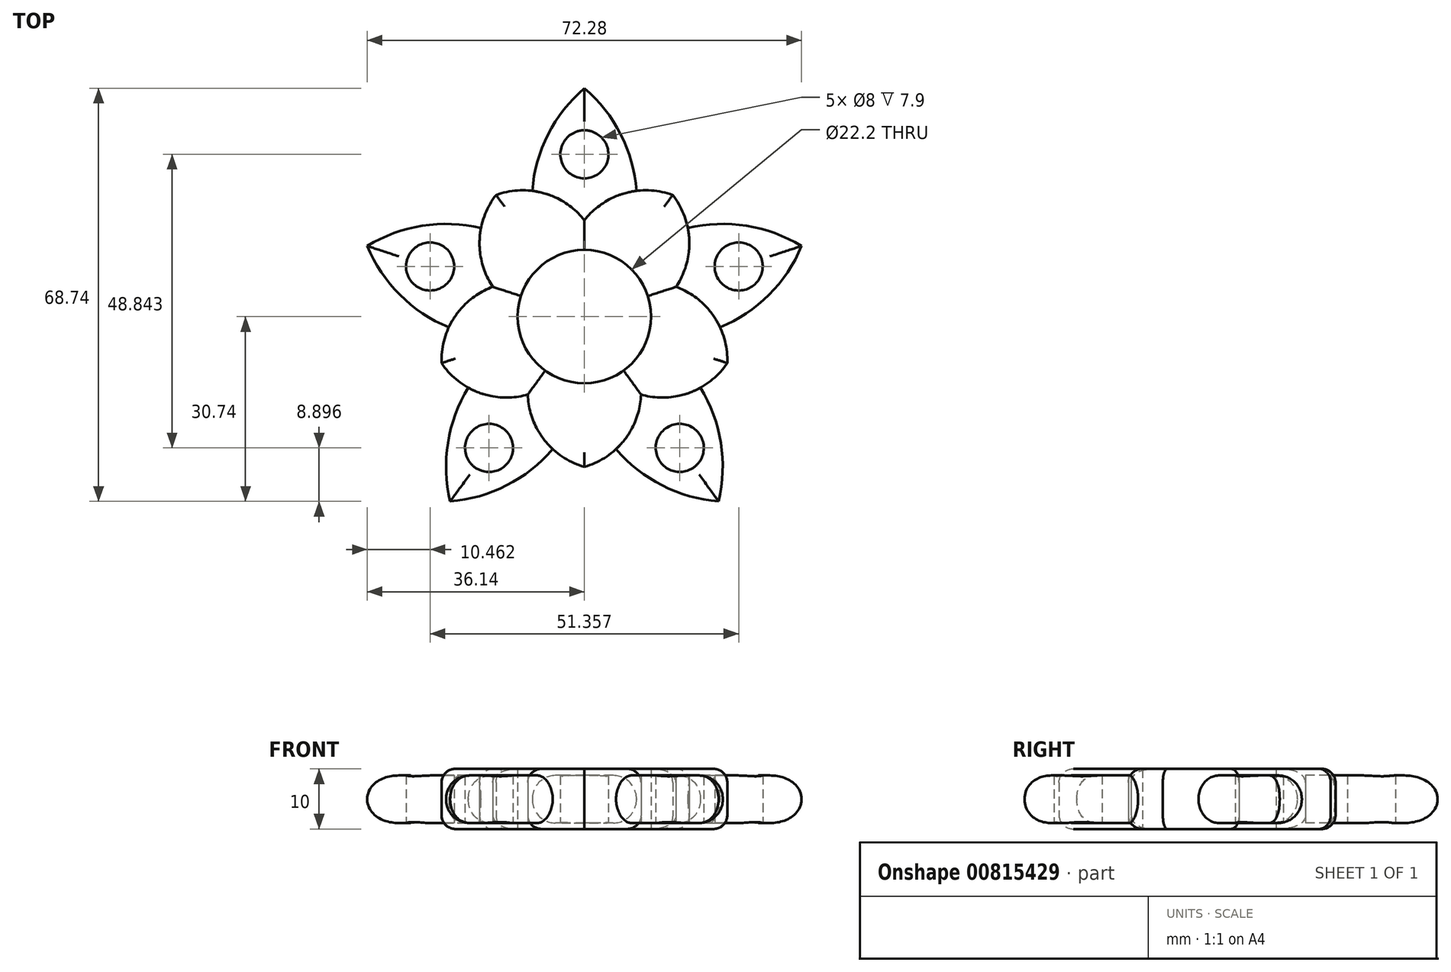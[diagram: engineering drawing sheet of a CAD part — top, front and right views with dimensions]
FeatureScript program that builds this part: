
annotation { "Feature Type Name" : "Feature", "Feature Type Description" : "" }
export const myFeature = defineFeature(function(context is Context, id is Id, definition is map)
    precondition{}
    {
        {
            var Q0;
            Q0=qCreatedBy(makeId("Top.planeOp"),FACE);
            var sketch = newSketch(context, id + "F0", { "sketchPlane" : qUnion([Q0])});
            skLineSegment(sketch, "E0", {"start": v(0, 0) * mm, "end": v(0, 38) * mm, "construction": true});
            skArc(sketch, "E1", {"start": v(0, 38) * mm, "mid": v(-8.75, 19) * mm, "end": v(0, 0) * mm});
            skArc(sketch, "E2", {"start": v(0, 0) * mm, "mid": v(8.75, 19) * mm, "end": v(0, 38) * mm});
            skLineSegment(sketch, "E3", {"start": v(0, 0) * mm, "end": v(0, -25) * mm, "construction": true});
            skArc(sketch, "E4", {"start": v(0, -25) * mm, "mid": v(9.43, -12.5) * mm, "end": v(0, 0) * mm});
            skArc(sketch, "E5", {"start": v(0, 0) * mm, "mid": v(-9.43, -12.5) * mm, "end": v(0, -25) * mm});
            skCircle(sketch, "E6", {"center": v(0, 0) * mm, "radius": 11.1 * mm});
            skArc(sketch, "E7.1.0", {"start": v(0, 0) * mm, "mid": v(-15.37, 14.2) * mm, "end": v(-36.14, 11.74) * mm});
            skArc(sketch, "E7.1.1", {"start": v(-36.14, 11.74) * mm, "mid": v(-20.77, -2.45) * mm, "end": v(0, 0) * mm});
            skArc(sketch, "E7.1.2", {"start": v(0, 0) * mm, "mid": v(8.97, -12.83) * mm, "end": v(23.78, -7.73) * mm});
            skArc(sketch, "E7.1.3", {"start": v(23.78, -7.73) * mm, "mid": v(14.8, 5.1) * mm, "end": v(0, 0) * mm});
            skArc(sketch, "E7.2.0", {"start": v(0, 0) * mm, "mid": v(-18.25, -10.23) * mm, "end": v(-22.34, -30.74) * mm});
            skArc(sketch, "E7.2.1", {"start": v(-22.34, -30.74) * mm, "mid": v(-4.09, -20.52) * mm, "end": v(0, 0) * mm});
            skArc(sketch, "E7.2.2", {"start": v(0, 0) * mm, "mid": v(14.98, 4.57) * mm, "end": v(14.7, 20.23) * mm});
            skArc(sketch, "E7.2.3", {"start": v(14.7, 20.23) * mm, "mid": v(-0.28, 15.66) * mm, "end": v(0, 0) * mm});
            skArc(sketch, "E7.3.0", {"start": v(0, 0) * mm, "mid": v(4.09, -20.52) * mm, "end": v(22.34, -30.74) * mm});
            skArc(sketch, "E7.3.1", {"start": v(22.34, -30.74) * mm, "mid": v(18.25, -10.23) * mm, "end": v(0, 0) * mm});
            skArc(sketch, "E7.3.2", {"start": v(0, 0) * mm, "mid": v(0.28, 15.66) * mm, "end": v(-14.7, 20.23) * mm});
            skArc(sketch, "E7.3.3", {"start": v(-14.7, 20.23) * mm, "mid": v(-14.98, 4.57) * mm, "end": v(0, 0) * mm});
            skArc(sketch, "E7.4.0", {"start": v(0, 0) * mm, "mid": v(20.77, -2.45) * mm, "end": v(36.14, 11.74) * mm});
            skArc(sketch, "E7.4.1", {"start": v(36.14, 11.74) * mm, "mid": v(15.37, 14.2) * mm, "end": v(0, 0) * mm});
            skArc(sketch, "E7.4.2", {"start": v(0, 0) * mm, "mid": v(-14.8, 5.1) * mm, "end": v(-23.78, -7.73) * mm});
            skArc(sketch, "E7.4.3", {"start": v(-23.78, -7.73) * mm, "mid": v(-8.97, -12.83) * mm, "end": v(0, 0) * mm});
            skCircle(sketch, "E8", {"center": v(0, 27) * mm, "radius": 4 * mm});
            skCircle(sketch, "E9.1.0", {"center": v(-25.68, 8.34) * mm, "radius": 4 * mm});
            skCircle(sketch, "E9.2.0", {"center": v(-15.87, -21.84) * mm, "radius": 4 * mm});
            skCircle(sketch, "E9.3.0", {"center": v(15.87, -21.84) * mm, "radius": 4 * mm});
            skCircle(sketch, "E9.4.0", {"center": v(25.68, 8.34) * mm, "radius": 4 * mm});
            skSolve(sketch);
        }
        {
            var Q0;
            {var subQ0=sQuery(id+"F0.wireOp",EDGE,"E2");var subQ1=sQuery(id+"F0.wireOp",EDGE,"E1");var subQ2=makeQuery(id+"F0.imprint","INTERSECT",VERTEX,{"derivedFrom":[subQ1,subQ0]});Q0=makeQuery(id+"F0.imprint","IMPRINT",FACE,{"disambiguationData":[TD([[makeQuery(id+"F0.imprint","IMPRINT",EDGE,{"disambiguationData":[TD([[subQ2,-1.0]])],"derivedFrom":subQ1}),1.0]])]});}
            var Q1;
            {var subQ0=sQuery(id+"F0.wireOp",EDGE,"E7.3.0");var subQ1=sQuery(id+"F0.wireOp",EDGE,"E4");var subQ2=makeQuery(id+"F0.imprint","INTERSECT",VERTEX,{"derivedFrom":[subQ1,subQ0]});Q1=makeQuery(id+"F0.imprint","IMPRINT",FACE,{"disambiguationData":[TD([[makeQuery(id+"F0.imprint","IMPRINT",EDGE,{"disambiguationData":[TD([[subQ2,-1.0]])],"derivedFrom":subQ1}),-1.0]])]});}
            var Q2;
            {var subQ0=sQuery(id+"F0.wireOp",EDGE,"E7.2.1");var subQ1=sQuery(id+"F0.wireOp",EDGE,"E5");var subQ2=makeQuery(id+"F0.imprint","INTERSECT",VERTEX,{"derivedFrom":[subQ1,subQ0]});Q2=makeQuery(id+"F0.imprint","IMPRINT",FACE,{"disambiguationData":[TD([[makeQuery(id+"F0.imprint","IMPRINT",EDGE,{"disambiguationData":[TD([[subQ2,1.0]])],"derivedFrom":subQ1}),-1.0]])]});}
            var Q3;
            {var subQ0=sQuery(id+"F0.wireOp",EDGE,"E7.1.1");var subQ1=sQuery(id+"F0.wireOp",EDGE,"E7.1.0");var subQ2=makeQuery(id+"F0.imprint","INTERSECT",VERTEX,{"derivedFrom":[subQ1,subQ0]});Q3=makeQuery(id+"F0.imprint","IMPRINT",FACE,{"disambiguationData":[TD([[makeQuery(id+"F0.imprint","IMPRINT",EDGE,{"disambiguationData":[TD([[subQ2,1.0]])],"derivedFrom":subQ1}),1.0]])]});}
            var Q4;
            {var subQ0=sQuery(id+"F0.wireOp",EDGE,"E7.4.0");var subQ1=sQuery(id+"F0.wireOp",EDGE,"E7.1.3");var subQ2=makeQuery(id+"F0.imprint","INTERSECT",VERTEX,{"derivedFrom":[subQ1,subQ0]});Q4=makeQuery(id+"F0.imprint","IMPRINT",FACE,{"disambiguationData":[TD([[makeQuery(id+"F0.imprint","IMPRINT",EDGE,{"disambiguationData":[TD([[subQ2,-1.0]])],"derivedFrom":subQ1}),-1.0]])]});}
            extrude(context, id + "F1", {"entities" : qUnion([Q0, Q1, Q2, Q3, Q4]), "depth" : 3.9 * mm, "offsetDistance" : 25 * mm, "hasSecondDirection" : true, "secondDirectionOppositeDirection" : true, "secondDirectionDepth" : 4 * mm});
        }
        {
            var Q0;
            {var subQ0=sQuery(id+"F0.wireOp",EDGE,"E7.3.2");var subQ1=sQuery(id+"F0.wireOp",EDGE,"E1");var subQ2=makeQuery(id+"F0.imprint","INTERSECT",VERTEX,{"derivedFrom":[subQ1,subQ0]});Q0=makeQuery(id+"F0.imprint","IMPRINT",FACE,{"disambiguationData":[TD([[makeQuery(id+"F0.imprint","IMPRINT",EDGE,{"disambiguationData":[TD([[subQ2,-1.0]])],"derivedFrom":subQ1}),-1.0]])]});}
            var Q1;
            {var subQ1=sQuery(id+"F0.wireOp",EDGE,"E1");var subQ7=sQuery(id+"F0.wireOp",EDGE,"E7.3.2");var subQ9=makeQuery(id+"F0.imprint","INTERSECT",VERTEX,{"derivedFrom":[subQ1,subQ7]});Q1=makeQuery(id+"F0.imprint","IMPRINT",FACE,{"disambiguationData":[TD([[makeQuery(id+"F0.imprint","IMPRINT",EDGE,{"disambiguationData":[TD([[subQ9,-1.0]])],"derivedFrom":subQ1}),1.0]])]});}
            var Q2;
            {var subQ1=sQuery(id+"F0.wireOp",EDGE,"E7.1.0");var subQ5=sQuery(id+"F0.wireOp",EDGE,"E1");var subQ6=makeQuery(id+"F0.imprint","INTERSECT",VERTEX,{"derivedFrom":[subQ5,subQ1]});Q2=makeQuery(id+"F0.imprint","IMPRINT",FACE,{"disambiguationData":[TD([[makeQuery(id+"F0.imprint","IMPRINT",EDGE,{"disambiguationData":[TD([[subQ6,-1.0]])],"derivedFrom":subQ5}),-1.0]])]});}
            var Q3;
            {var subQ1=sQuery(id+"F0.wireOp",EDGE,"E7.1.2");var subQ3=sQuery(id+"F0.wireOp",EDGE,"E4");var subQ4=makeQuery(id+"F0.imprint","INTERSECT",VERTEX,{"derivedFrom":[subQ3,subQ1]});Q3=makeQuery(id+"F0.imprint","IMPRINT",FACE,{"disambiguationData":[TD([[makeQuery(id+"F0.imprint","IMPRINT",EDGE,{"disambiguationData":[TD([[subQ4,-1.0]])],"derivedFrom":subQ3}),-1.0]])]});}
            var Q4;
            {var subQ5=sQuery(id+"F0.wireOp",EDGE,"E6");var subQ6=sQuery(id+"F0.wireOp",EDGE,"E5");var subQ7=makeQuery(id+"F0.imprint","INTERSECT",VERTEX,{"derivedFrom":[subQ6,subQ5]});Q4=makeQuery(id+"F0.imprint","IMPRINT",FACE,{"disambiguationData":[TD([[makeQuery(id+"F0.imprint","IMPRINT",EDGE,{"disambiguationData":[TD([[subQ7,-1.0]])],"derivedFrom":subQ6}),-1.0]])]});}
            var Q5;
            {var subQ1=sQuery(id+"F0.wireOp",EDGE,"E6");var subQ5=sQuery(id+"F0.wireOp",EDGE,"E7.2.2");var subQ6=makeQuery(id+"F0.imprint","INTERSECT",VERTEX,{"derivedFrom":[subQ1,subQ5]});Q5=makeQuery(id+"F0.imprint","IMPRINT",FACE,{"disambiguationData":[TD([[makeQuery(id+"F0.imprint","IMPRINT",EDGE,{"disambiguationData":[TD([[subQ6,1.0]])],"derivedFrom":subQ1}),-1.0]])]});}
            var Q6;
            {var subQ0=sQuery(id+"F0.wireOp",EDGE,"E5");var subQ1=sQuery(id+"F0.wireOp",EDGE,"E4");var subQ2=makeQuery(id+"F0.imprint","INTERSECT",VERTEX,{"derivedFrom":[subQ1,subQ0]});Q6=makeQuery(id+"F0.imprint","IMPRINT",FACE,{"disambiguationData":[TD([[makeQuery(id+"F0.imprint","IMPRINT",EDGE,{"disambiguationData":[TD([[subQ2,-1.0]])],"derivedFrom":subQ1}),1.0]])]});}
            var Q7;
            {var subQ0=sQuery(id+"F0.wireOp",EDGE,"E7.4.2");var subQ1=sQuery(id+"F0.wireOp",EDGE,"E7.1.1");var subQ2=makeQuery(id+"F0.imprint","INTERSECT",VERTEX,{"derivedFrom":[subQ1,subQ0]});Q7=makeQuery(id+"F0.imprint","IMPRINT",FACE,{"disambiguationData":[TD([[makeQuery(id+"F0.imprint","IMPRINT",EDGE,{"disambiguationData":[TD([[subQ2,-1.0]])],"derivedFrom":subQ1}),-1.0]])]});}
            var Q8;
            {var subQ0=sQuery(id+"F0.wireOp",EDGE,"E7.1.2");var subQ1=sQuery(id+"F0.wireOp",EDGE,"E4");var subQ2=makeQuery(id+"F0.imprint","INTERSECT",VERTEX,{"derivedFrom":[subQ1,subQ0]});Q8=makeQuery(id+"F0.imprint","IMPRINT",FACE,{"disambiguationData":[TD([[makeQuery(id+"F0.imprint","IMPRINT",EDGE,{"disambiguationData":[TD([[subQ2,-1.0]])],"derivedFrom":subQ1}),1.0]])]});}
            var Q9;
            {var subQ0=sQuery(id+"F0.wireOp",EDGE,"E7.3.3");var subQ1=sQuery(id+"F0.wireOp",EDGE,"E6");var subQ2=makeQuery(id+"F0.imprint","INTERSECT",VERTEX,{"derivedFrom":[subQ1,subQ0]});Q9=makeQuery(id+"F0.imprint","IMPRINT",FACE,{"disambiguationData":[TD([[makeQuery(id+"F0.imprint","IMPRINT",EDGE,{"disambiguationData":[TD([[subQ2,-1.0]])],"derivedFrom":subQ1}),-1.0]])]});}
            var Q10;
            {var subQ0=sQuery(id+"F0.wireOp",EDGE,"E7.1.3");var subQ1=sQuery(id+"F0.wireOp",EDGE,"E7.1.2");var subQ2=makeQuery(id+"F0.imprint","INTERSECT",VERTEX,{"derivedFrom":[subQ1,subQ0]});Q10=makeQuery(id+"F0.imprint","IMPRINT",FACE,{"disambiguationData":[TD([[makeQuery(id+"F0.imprint","IMPRINT",EDGE,{"disambiguationData":[TD([[subQ2,1.0]])],"derivedFrom":subQ1}),1.0]])]});}
            var Q11;
            {var subQ1=sQuery(id+"F0.wireOp",EDGE,"E4");var subQ5=sQuery(id+"F0.wireOp",EDGE,"E7.3.0");var subQ6=makeQuery(id+"F0.imprint","INTERSECT",VERTEX,{"derivedFrom":[subQ1,subQ5]});Q11=makeQuery(id+"F0.imprint","IMPRINT",FACE,{"disambiguationData":[TD([[makeQuery(id+"F0.imprint","IMPRINT",EDGE,{"disambiguationData":[TD([[subQ6,-1.0]])],"derivedFrom":subQ1}),1.0]])]});}
            var Q12;
            {var subQ3=sQuery(id+"F0.wireOp",EDGE,"E7.2.1");var subQ5=sQuery(id+"F0.wireOp",EDGE,"E5");var subQ6=makeQuery(id+"F0.imprint","INTERSECT",VERTEX,{"derivedFrom":[subQ5,subQ3]});Q12=makeQuery(id+"F0.imprint","IMPRINT",FACE,{"disambiguationData":[TD([[makeQuery(id+"F0.imprint","IMPRINT",EDGE,{"disambiguationData":[TD([[subQ6,1.0]])],"derivedFrom":subQ5}),1.0]])]});}
            var Q13;
            {var subQ0=sQuery(id+"F0.wireOp",EDGE,"E6");var subQ1=sQuery(id+"F0.wireOp",EDGE,"E5");var subQ2=makeQuery(id+"F0.imprint","INTERSECT",VERTEX,{"derivedFrom":[subQ1,subQ0]});Q13=makeQuery(id+"F0.imprint","IMPRINT",FACE,{"disambiguationData":[TD([[makeQuery(id+"F0.imprint","IMPRINT",EDGE,{"disambiguationData":[TD([[subQ2,-1.0]])],"derivedFrom":subQ1}),1.0]])]});}
            var Q14;
            {var subQ0=sQuery(id+"F0.wireOp",EDGE,"E7.1.3");var subQ1=sQuery(id+"F0.wireOp",EDGE,"E6");var subQ2=makeQuery(id+"F0.imprint","INTERSECT",VERTEX,{"derivedFrom":[subQ1,subQ0]});Q14=makeQuery(id+"F0.imprint","IMPRINT",FACE,{"disambiguationData":[TD([[makeQuery(id+"F0.imprint","IMPRINT",EDGE,{"disambiguationData":[TD([[subQ2,1.0]])],"derivedFrom":subQ1}),-1.0]])]});}
            var Q15;
            {var subQ3=sQuery(id+"F0.wireOp",EDGE,"E7.2.3");var subQ5=sQuery(id+"F0.wireOp",EDGE,"E2");var subQ6=makeQuery(id+"F0.imprint","INTERSECT",VERTEX,{"derivedFrom":[subQ5,subQ3]});Q15=makeQuery(id+"F0.imprint","IMPRINT",FACE,{"disambiguationData":[TD([[makeQuery(id+"F0.imprint","IMPRINT",EDGE,{"disambiguationData":[TD([[subQ6,1.0]])],"derivedFrom":subQ5}),1.0]])]});}
            var Q16;
            {var subQ0=sQuery(id+"F0.wireOp",EDGE,"E7.2.0");var subQ1=sQuery(id+"F0.wireOp",EDGE,"E6");var subQ2=makeQuery(id+"F0.imprint","INTERSECT",VERTEX,{"derivedFrom":[subQ1,subQ0]});Q16=makeQuery(id+"F0.imprint","IMPRINT",FACE,{"disambiguationData":[TD([[makeQuery(id+"F0.imprint","IMPRINT",EDGE,{"disambiguationData":[TD([[subQ2,-1.0]])],"derivedFrom":subQ1}),-1.0]])]});}
            var Q17;
            {var subQ0=sQuery(id+"F0.wireOp",EDGE,"E7.1.0");var subQ1=sQuery(id+"F0.wireOp",EDGE,"E1");var subQ2=makeQuery(id+"F0.imprint","INTERSECT",VERTEX,{"derivedFrom":[subQ1,subQ0]});Q17=makeQuery(id+"F0.imprint","IMPRINT",FACE,{"disambiguationData":[TD([[makeQuery(id+"F0.imprint","IMPRINT",EDGE,{"disambiguationData":[TD([[subQ2,-1.0]])],"derivedFrom":subQ1}),1.0]])]});}
            var Q18;
            {var subQ1=sQuery(id+"F0.wireOp",EDGE,"E6");var subQ7=sQuery(id+"F0.wireOp",EDGE,"E2");var subQ8=makeQuery(id+"F0.imprint","INTERSECT",VERTEX,{"derivedFrom":[subQ7,subQ1]});Q18=makeQuery(id+"F0.imprint","IMPRINT",FACE,{"disambiguationData":[TD([[makeQuery(id+"F0.imprint","IMPRINT",EDGE,{"disambiguationData":[TD([[subQ8,-1.0]])],"derivedFrom":subQ7}),-1.0]])]});}
            var Q19;
            {var subQ0=sQuery(id+"F0.wireOp",EDGE,"E7.2.3");var subQ1=sQuery(id+"F0.wireOp",EDGE,"E2");var subQ2=makeQuery(id+"F0.imprint","INTERSECT",VERTEX,{"derivedFrom":[subQ1,subQ0]});Q19=makeQuery(id+"F0.imprint","IMPRINT",FACE,{"disambiguationData":[TD([[makeQuery(id+"F0.imprint","IMPRINT",EDGE,{"disambiguationData":[TD([[subQ2,1.0]])],"derivedFrom":subQ1}),-1.0]])]});}
            var Q20;
            {var subQ0=sQuery(id+"F0.wireOp",EDGE,"E7.4.0");var subQ1=sQuery(id+"F0.wireOp",EDGE,"E6");var subQ2=makeQuery(id+"F0.imprint","INTERSECT",VERTEX,{"derivedFrom":[subQ1,subQ0]});Q20=makeQuery(id+"F0.imprint","IMPRINT",FACE,{"disambiguationData":[TD([[makeQuery(id+"F0.imprint","IMPRINT",EDGE,{"disambiguationData":[TD([[subQ2,-1.0]])],"derivedFrom":subQ1}),-1.0]])]});}
            var Q21;
            {var subQ0=sQuery(id+"F0.wireOp",EDGE,"E7.3.0");var subQ1=sQuery(id+"F0.wireOp",EDGE,"E6");var subQ2=makeQuery(id+"F0.imprint","INTERSECT",VERTEX,{"derivedFrom":[subQ1,subQ0]});Q21=makeQuery(id+"F0.imprint","IMPRINT",FACE,{"disambiguationData":[TD([[makeQuery(id+"F0.imprint","IMPRINT",EDGE,{"disambiguationData":[TD([[subQ2,-1.0]])],"derivedFrom":subQ1}),-1.0]])]});}
            var Q22;
            {var subQ0=sQuery(id+"F0.wireOp",EDGE,"E7.4.2");var subQ1=sQuery(id+"F0.wireOp",EDGE,"E6");var subQ2=makeQuery(id+"F0.imprint","INTERSECT",VERTEX,{"derivedFrom":[subQ1,subQ0]});Q22=makeQuery(id+"F0.imprint","IMPRINT",FACE,{"disambiguationData":[TD([[makeQuery(id+"F0.imprint","IMPRINT",EDGE,{"disambiguationData":[TD([[subQ2,-1.0]])],"derivedFrom":subQ1}),-1.0]])]});}
            var Q23;
            {var subQ0=sQuery(id+"F0.wireOp",EDGE,"E7.3.2");var subQ1=sQuery(id+"F0.wireOp",EDGE,"E6");var subQ2=makeQuery(id+"F0.imprint","INTERSECT",VERTEX,{"derivedFrom":[subQ1,subQ0]});Q23=makeQuery(id+"F0.imprint","IMPRINT",FACE,{"disambiguationData":[TD([[makeQuery(id+"F0.imprint","IMPRINT",EDGE,{"disambiguationData":[TD([[subQ2,-1.0]])],"derivedFrom":subQ1}),-1.0]])]});}
            var Q24;
            {var subQ0=sQuery(id+"F0.wireOp",EDGE,"E6");var subQ1=sQuery(id+"F0.wireOp",EDGE,"E2");var subQ2=makeQuery(id+"F0.imprint","INTERSECT",VERTEX,{"derivedFrom":[subQ1,subQ0]});Q24=makeQuery(id+"F0.imprint","IMPRINT",FACE,{"disambiguationData":[TD([[makeQuery(id+"F0.imprint","IMPRINT",EDGE,{"disambiguationData":[TD([[subQ2,-1.0]])],"derivedFrom":subQ1}),1.0]])]});}
            extrude(context, id + "F2", {"entities" : qUnion([Q0, Q1, Q2, Q3, Q4, Q5, Q6, Q7, Q8, Q9, Q10, Q11, Q12, Q13, Q14, Q15, Q16, Q17, Q18, Q19, Q20, Q21, Q22, Q23, Q24]), "depth" : 5 * mm, "offsetDistance" : 25 * mm, "hasSecondDirection" : true, "secondDirectionOppositeDirection" : true, "secondDirectionDepth" : 5 * mm});
        }
        {
            var Q0;
            Q0=makeQuery(id+"F2.opExtrude","CAP_EDGE",EDGE,{"disambiguationData":[OSD([sQuery(id+"F0.wireOp",EDGE,"E7.4.2")])],"isStart":false});
            var Q1;
            Q1=makeQuery(id+"F2.opExtrude","CAP_EDGE",EDGE,{"disambiguationData":[OSD([sQuery(id+"F0.wireOp",EDGE,"E7.4.3")])],"isStart":false});
            var Q2;
            Q2=makeQuery(id+"F2.opExtrude","CAP_EDGE",EDGE,{"disambiguationData":[OSD([sQuery(id+"F0.wireOp",EDGE,"E5")])],"isStart":false});
            var Q3;
            Q3=makeQuery(id+"F2.opExtrude","CAP_EDGE",EDGE,{"disambiguationData":[OSD([sQuery(id+"F0.wireOp",EDGE,"E4")])],"isStart":false});
            var Q4;
            Q4=makeQuery(id+"F2.opExtrude","CAP_EDGE",EDGE,{"disambiguationData":[OSD([sQuery(id+"F0.wireOp",EDGE,"E7.1.3")])],"isStart":false});
            var Q5;
            Q5=makeQuery(id+"F2.opExtrude","CAP_EDGE",EDGE,{"disambiguationData":[OSD([sQuery(id+"F0.wireOp",EDGE,"E7.2.2")])],"isStart":false});
            var Q6;
            Q6=makeQuery(id+"F2.opExtrude","CAP_EDGE",EDGE,{"disambiguationData":[OSD([sQuery(id+"F0.wireOp",EDGE,"E7.2.3")])],"isStart":false});
            var Q7;
            Q7=makeQuery(id+"F2.opExtrude","CAP_EDGE",EDGE,{"disambiguationData":[OSD([sQuery(id+"F0.wireOp",EDGE,"E7.3.3")])],"isStart":false});
            var Q8;
            Q8=makeQuery(id+"F2.opExtrude","CAP_EDGE",EDGE,{"disambiguationData":[OSD([sQuery(id+"F0.wireOp",EDGE,"E7.3.2")])],"isStart":false});
            var Q9;
            Q9=makeQuery(id+"F2.opExtrude","CAP_EDGE",EDGE,{"disambiguationData":[OSD([sQuery(id+"F0.wireOp",EDGE,"E7.1.2")])],"isStart":false});
            var Q10;
            Q10=makeQuery(id+"F2.opExtrude","CAP_EDGE",EDGE,{"disambiguationData":[OSD([sQuery(id+"F0.wireOp",EDGE,"E7.3.3")])],"isStart":true});
            var Q11;
            Q11=makeQuery(id+"F2.opExtrude","CAP_EDGE",EDGE,{"disambiguationData":[OSD([sQuery(id+"F0.wireOp",EDGE,"E7.4.2")])],"isStart":true});
            var Q12;
            Q12=makeQuery(id+"F2.opExtrude","CAP_EDGE",EDGE,{"disambiguationData":[OSD([sQuery(id+"F0.wireOp",EDGE,"E7.4.3")])],"isStart":true});
            var Q13;
            Q13=makeQuery(id+"F2.opExtrude","CAP_EDGE",EDGE,{"disambiguationData":[OSD([sQuery(id+"F0.wireOp",EDGE,"E5")])],"isStart":true});
            var Q14;
            Q14=makeQuery(id+"F2.opExtrude","CAP_EDGE",EDGE,{"disambiguationData":[OSD([sQuery(id+"F0.wireOp",EDGE,"E4")])],"isStart":true});
            var Q15;
            Q15=makeQuery(id+"F2.opExtrude","CAP_EDGE",EDGE,{"disambiguationData":[OSD([sQuery(id+"F0.wireOp",EDGE,"E7.1.2")])],"isStart":true});
            var Q16;
            Q16=makeQuery(id+"F2.opExtrude","CAP_EDGE",EDGE,{"disambiguationData":[OSD([sQuery(id+"F0.wireOp",EDGE,"E7.1.3")])],"isStart":true});
            var Q17;
            Q17=makeQuery(id+"F2.opExtrude","CAP_EDGE",EDGE,{"disambiguationData":[OSD([sQuery(id+"F0.wireOp",EDGE,"E7.2.2")])],"isStart":true});
            var Q18;
            Q18=makeQuery(id+"F2.opExtrude","CAP_EDGE",EDGE,{"disambiguationData":[OSD([sQuery(id+"F0.wireOp",EDGE,"E7.2.3")])],"isStart":true});
            var Q19;
            Q19=makeQuery(id+"F2.opExtrude","CAP_EDGE",EDGE,{"disambiguationData":[OSD([sQuery(id+"F0.wireOp",EDGE,"E7.3.2")])],"isStart":true});
            fillet(context, id + "F3", {"entities" : qUnion([Q0, Q1, Q2, Q3, Q4, Q5, Q6, Q7, Q8, Q9, Q10, Q11, Q12, Q13, Q14, Q15, Q16, Q17, Q18, Q19]), "radius" : 2.3 * mm, "tangentPropagation" : true, "allowEdgeOverflow" : false});
        }
        {
            var Q0;
            Q0=makeQuery(id+"F1.opExtrude","CAP_EDGE",EDGE,{"disambiguationData":[OSD([sQuery(id+"F0.wireOp",EDGE,"E7.4.0")])],"isStart":true});
            var Q1;
            Q1=makeQuery(id+"F1.opExtrude","CAP_EDGE",EDGE,{"disambiguationData":[OSD([sQuery(id+"F0.wireOp",EDGE,"E7.4.1")])],"isStart":true});
            var Q2;
            Q2=makeQuery(id+"F1.opExtrude","CAP_EDGE",EDGE,{"disambiguationData":[OSD([sQuery(id+"F0.wireOp",EDGE,"E1")])],"isStart":true});
            var Q3;
            Q3=makeQuery(id+"F1.opExtrude","CAP_EDGE",EDGE,{"disambiguationData":[OSD([sQuery(id+"F0.wireOp",EDGE,"E7.1.0")])],"isStart":true});
            var Q4;
            Q4=makeQuery(id+"F1.opExtrude","CAP_EDGE",EDGE,{"disambiguationData":[OSD([sQuery(id+"F0.wireOp",EDGE,"E7.1.1")])],"isStart":true});
            var Q5;
            Q5=makeQuery(id+"F1.opExtrude","CAP_EDGE",EDGE,{"disambiguationData":[OSD([sQuery(id+"F0.wireOp",EDGE,"E7.2.1")])],"isStart":true});
            var Q6;
            Q6=makeQuery(id+"F1.opExtrude","CAP_EDGE",EDGE,{"disambiguationData":[OSD([sQuery(id+"F0.wireOp",EDGE,"E7.3.0")])],"isStart":true});
            var Q7;
            Q7=makeQuery(id+"F1.opExtrude","CAP_EDGE",EDGE,{"disambiguationData":[OSD([sQuery(id+"F0.wireOp",EDGE,"E7.3.1")])],"isStart":true});
            var Q8;
            Q8=makeQuery(id+"F1.opExtrude","CAP_EDGE",EDGE,{"disambiguationData":[OSD([sQuery(id+"F0.wireOp",EDGE,"E7.2.0")])],"isStart":true});
            var Q9;
            Q9=makeQuery(id+"F1.opExtrude","CAP_EDGE",EDGE,{"disambiguationData":[OSD([sQuery(id+"F0.wireOp",EDGE,"E2")])],"isStart":true});
            var Q10;
            Q10=makeQuery(id+"F1.opExtrude","CAP_EDGE",EDGE,{"disambiguationData":[OSD([sQuery(id+"F0.wireOp",EDGE,"E1")])],"isStart":false});
            var Q11;
            Q11=makeQuery(id+"F1.opExtrude","CAP_EDGE",EDGE,{"disambiguationData":[OSD([sQuery(id+"F0.wireOp",EDGE,"E2")])],"isStart":false});
            var Q12;
            Q12=makeQuery(id+"F1.opExtrude","CAP_EDGE",EDGE,{"disambiguationData":[OSD([sQuery(id+"F0.wireOp",EDGE,"E7.1.1")])],"isStart":false});
            var Q13;
            Q13=makeQuery(id+"F1.opExtrude","CAP_EDGE",EDGE,{"disambiguationData":[OSD([sQuery(id+"F0.wireOp",EDGE,"E7.2.0")])],"isStart":false});
            var Q14;
            Q14=makeQuery(id+"F1.opExtrude","CAP_EDGE",EDGE,{"disambiguationData":[OSD([sQuery(id+"F0.wireOp",EDGE,"E7.2.1")])],"isStart":false});
            var Q15;
            Q15=makeQuery(id+"F1.opExtrude","CAP_EDGE",EDGE,{"disambiguationData":[OSD([sQuery(id+"F0.wireOp",EDGE,"E7.1.0")])],"isStart":false});
            var Q16;
            Q16=makeQuery(id+"F1.opExtrude","CAP_EDGE",EDGE,{"disambiguationData":[OSD([sQuery(id+"F0.wireOp",EDGE,"E7.3.0")])],"isStart":false});
            var Q17;
            Q17=makeQuery(id+"F1.opExtrude","CAP_EDGE",EDGE,{"disambiguationData":[OSD([sQuery(id+"F0.wireOp",EDGE,"E7.3.1")])],"isStart":false});
            var Q18;
            Q18=makeQuery(id+"F1.opExtrude","CAP_EDGE",EDGE,{"disambiguationData":[OSD([sQuery(id+"F0.wireOp",EDGE,"E7.4.0")])],"isStart":false});
            var Q19;
            Q19=makeQuery(id+"F1.opExtrude","CAP_EDGE",EDGE,{"disambiguationData":[OSD([sQuery(id+"F0.wireOp",EDGE,"E7.4.1")])],"isStart":false});
            fillet(context, id + "F4", {"entities" : qUnion([Q0, Q1, Q2, Q3, Q4, Q5, Q6, Q7, Q8, Q9, Q10, Q11, Q12, Q13, Q14, Q15, Q16, Q17, Q18, Q19]), "radius" : 3.9 * mm, "tangentPropagation" : true, "allowEdgeOverflow" : false});
        }
    });
